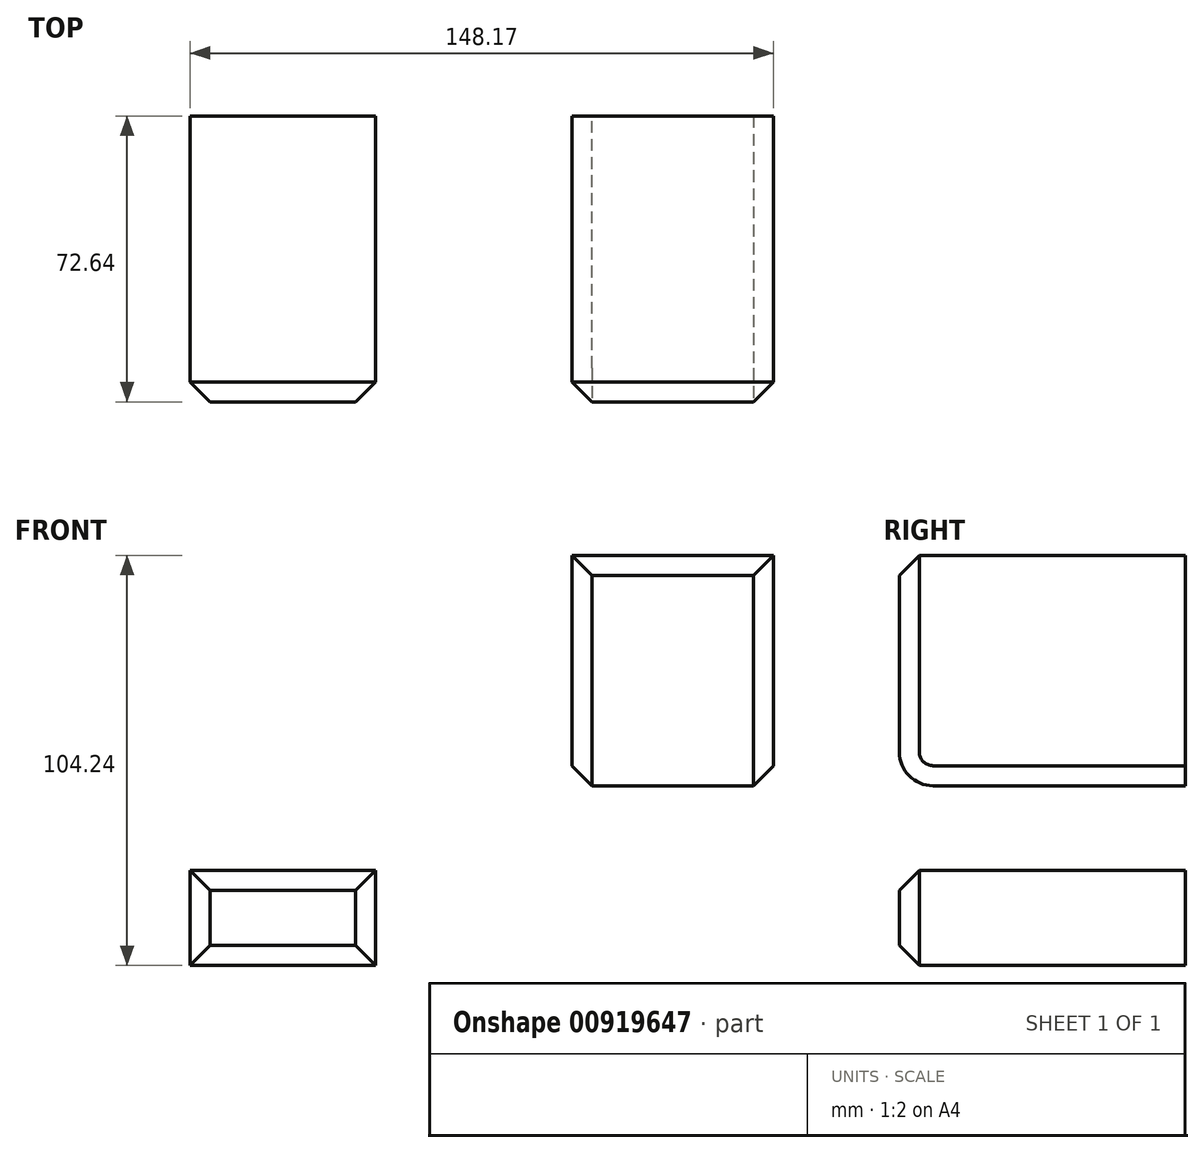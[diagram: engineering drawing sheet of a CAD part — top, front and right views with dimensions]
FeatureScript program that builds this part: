
annotation { "Feature Type Name" : "Feature", "Feature Type Description" : "" }
export const myFeature = defineFeature(function(context is Context, id is Id, definition is map)
    precondition{}
    {
        {
            var Q0;
            Q0=qCreatedBy(makeId("Front.planeOp"),FACE);
            var sketch = newSketch(context, id + "F0", { "sketchPlane" : qUnion([Q0])});
            skLineSegment(sketch, "E0.bottom", {"start": v(59.94, -25.92) * mm, "end": v(-58.49, -25.92) * mm});
            skLineSegment(sketch, "E0.top", {"start": v(59.94, 63.99) * mm, "end": v(-58.49, 63.99) * mm});
            skLineSegment(sketch, "E0.left", {"start": v(59.94, -25.92) * mm, "end": v(59.94, 63.99) * mm});
            skLineSegment(sketch, "E0.right", {"start": v(-58.49, -25.92) * mm, "end": v(-58.49, 63.99) * mm});
            skLineSegment(sketch, "E1.bottom", {"start": v(-37.04, -25.92) * mm, "end": v(10.05, -25.92) * mm});
            skLineSegment(sketch, "E1.top", {"start": v(-37.04, -50.1) * mm, "end": v(10.05, -50.1) * mm});
            skLineSegment(sketch, "E1.left", {"start": v(-37.04, -25.92) * mm, "end": v(-37.04, -50.1) * mm});
            skLineSegment(sketch, "E1.right", {"start": v(10.05, -25.92) * mm, "end": v(10.05, -50.1) * mm});
            skLineSegment(sketch, "E2.bottom", {"start": v(59.94, -4.4) * mm, "end": v(111.13, -4.4) * mm});
            skLineSegment(sketch, "E2.top", {"start": v(59.94, 54.14) * mm, "end": v(111.13, 54.14) * mm});
            skLineSegment(sketch, "E2.left", {"start": v(59.94, -4.4) * mm, "end": v(59.94, 54.14) * mm});
            skLineSegment(sketch, "E2.right", {"start": v(111.13, -4.4) * mm, "end": v(111.13, 54.14) * mm});
            skSolve(sketch);
        }
        {
            var Q0;
            Q0=makeQuery(id+"F0.imprint","IMPRINT",FACE,{"disambiguationData":[TD([[makeQuery(id+"F0.imprint","IMPRINT",EDGE,{"derivedFrom":sQuery(id+"F0.wireOp",EDGE,"E1.top")}),1.0]])]});
            var Q1;
            {var subQ0=sQuery(id+"F0.wireOp",EDGE,"E0.top");Q1=makeQuery(id+"F0.imprint","IMPRINT",FACE,{"disambiguationData":[TD([[makeQuery(id+"F0.imprint","IMPRINT",EDGE,{"derivedFrom":subQ0}),1.0]])]});}
            var Q2;
            {var subQ0=sQuery(id+"F0.wireOp",EDGE,"E2.bottom");Q2=makeQuery(id+"F0.imprint","IMPRINT",FACE,{"disambiguationData":[TD([[makeQuery(id+"F0.imprint","IMPRINT",EDGE,{"derivedFrom":subQ0}),1.0]])]});}
            extrude(context, id + "F1", {"entities" : qUnion([Q0, Q1, Q2]), "depth" : 72.64 * mm, "offsetDistance" : 25.4 * mm});
        }
        {
            var Q0;
            Q0=makeQuery(id+"F1.opExtrude","CAP_EDGE",EDGE,{"disambiguationData":[OSD([sQuery(id+"F0.wireOp",EDGE,"E2.bottom")])],"isStart":false});
            fillet(context, id + "F2", {"entities" : qUnion([Q0]), "radius" : 8.58 * mm, "tangentPropagation" : true, "allowEdgeOverflow" : false});
        }
        {
            var Q0;
            Q0=makeQuery(id+"F1.opExtrude","CAP_FACE",FACE,{"disambiguationData":[OSD([sQuery(id+"F0.wireOp",EDGE,"E0.bottom"),sQuery(id+"F0.wireOp",EDGE,"E0.top"),sQuery(id+"F0.wireOp",EDGE,"E0.left"),sQuery(id+"F0.wireOp",EDGE,"E0.right"),sQuery(id+"F0.wireOp",EDGE,"E1.top"),sQuery(id+"F0.wireOp",EDGE,"E1.left"),sQuery(id+"F0.wireOp",EDGE,"E1.right"),sQuery(id+"F0.wireOp",EDGE,"E2.bottom"),sQuery(id+"F0.wireOp",EDGE,"E2.top"),sQuery(id+"F0.wireOp",EDGE,"E2.right")])],"isStart":false});
            chamfer(context, id + "F3", {"entities" : qUnion([Q0]), "width" : 5.08 * mm, "tangentPropagation" : true});
        }
    });
